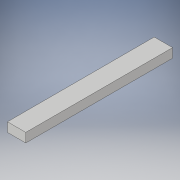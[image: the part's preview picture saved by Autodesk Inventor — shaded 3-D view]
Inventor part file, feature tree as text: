
AUTODESK INVENTOR PART (.ipt)
format: ipt  version: 2017 (Build 210142000, 142)  size: 91,648 bytes
history: native  units: in
note: dims shown in document units (in); Inventor stores cm internally (conversion verified against a paired STEP export)
features: extrude x1, sketch x1
ambient origin geometry x8: Origin, YZ Plane, XZ Plane, XY Plane, X Axis, Y Axis, Z Axis, Center Point
bodies: Solid1 (feature_tree)
feature tree (2):
  extrude  "Extrusion1"  Depth=16.0in
  sketch  "Sketch1"  dims[d0=2.0in d1=16.0in d2=1.0in d3=0.0in]
